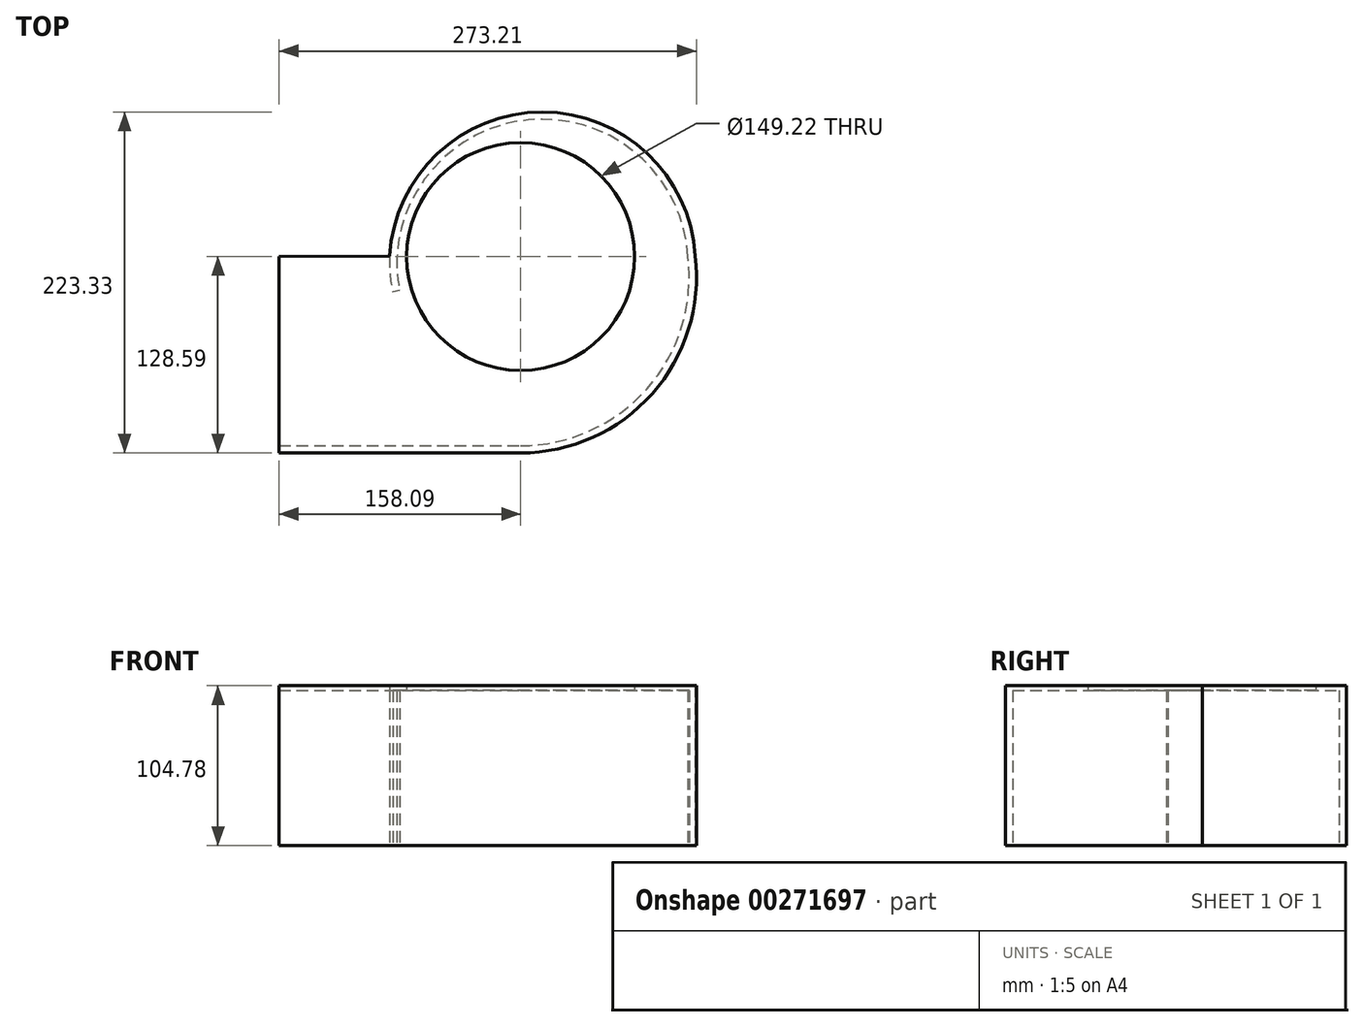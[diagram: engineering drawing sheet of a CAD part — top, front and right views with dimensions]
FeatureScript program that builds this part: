
annotation { "Feature Type Name" : "Feature", "Feature Type Description" : "" }
export const myFeature = defineFeature(function(context is Context, id is Id, definition is map)
    precondition{}
    {
        {
            var Q0;
            Q0=qCreatedBy(makeId("Top.planeOp"),FACE);
            var sketch = newSketch(context, id + "F3", { "sketchPlane" : qUnion([Q0])});
            skCircle(sketch, "E0", {"center": v(0, 0) * mm, "radius": 74.61 * mm, "construction": true});
            skPoint(sketch, "E1", {"position": v(-80.98, 0) * mm});
            skPoint(sketch, "E2", {"position": v(0, 88.9) * mm});
            skPoint(sketch, "E3", {"position": v(109.54, 0) * mm});
            skPoint(sketch, "E4", {"position": v(0, -123.83) * mm});
            skPoint(sketch, "E5", {"position": v(-138.11, 0) * mm});
            skArc(sketch, "E6", {"start": v(109.54, 0) * mm, "mid": v(14.28, 89.97) * mm, "end": v(-80.98, 0) * mm});
            skArc(sketch, "E7", {"start": v(-80.98, 0) * mm, "mid": v(-80.8, -11.18) * mm, "end": v(-79.04, -22.23) * mm});
            skLineSegment(sketch, "E8", {"start": v(-158.09, -123.83) * mm, "end": v(0, -123.83) * mm});
            skArc(sketch, "E9.trimOffspring", {"start": v(0, -123.83) * mm, "mid": v(82.66, -86.59) * mm, "end": v(109.54, 0) * mm});
            skArc(sketch, "E10.0", {"start": v(-85.73, 0.27) * mm, "mid": v(-85.55, -11.6) * mm, "end": v(-83.68, -23.31) * mm});
            skArc(sketch, "E10.1", {"start": v(114.28, 0.43) * mm, "mid": v(14.2, 94.74) * mm, "end": v(-85.73, 0.27) * mm});
            skArc(sketch, "E10.2", {"start": v(0, -128.59) * mm, "mid": v(86.18, -89.8) * mm, "end": v(114.28, 0.43) * mm});
            skLineSegment(sketch, "E11", {"start": v(-79.04, -22.23) * mm, "end": v(-83.68, -23.31) * mm});
            skPoint(sketch, "E12.end.orphan", {"position": v(-79.04, -123.83) * mm});
            skPoint(sketch, "E13.orphan", {"position": v(74.61, 0) * mm});
            skLineSegment(sketch, "E14.0", {"start": v(-158.09, -128.59) * mm, "end": v(0, -128.59) * mm});
            skLineSegment(sketch, "E15", {"start": v(-158.09, -128.59) * mm, "end": v(-158.09, -123.83) * mm});
            skSolve(sketch);
        }
        {
            var Q0;
            Q0=makeQuery(id+"F3.imprint","IMPRINT",FACE,{"disambiguationData":[TD([[makeQuery(id+"F3.imprint","IMPRINT",EDGE,{"derivedFrom":sQuery(id+"F3.wireOp",EDGE,"E6")}),-1.0]])]});
            var Q1;
            Q1=sQuery(id+"F3.wireOp",EDGE,"E10.1");
            var Q2;
            Q2=sQuery(id+"F3.wireOp",EDGE,"E6");
            var Q3;
            Q3=sQuery(id+"F3.wireOp",EDGE,"E9.trimOffspring");
            var Q4;
            Q4=sQuery(id+"F3.wireOp",EDGE,"E10.2");
            var Q5;
            Q5=sQuery(id+"F3.wireOp",EDGE,"E7");
            var Q6;
            Q6=sQuery(id+"F3.wireOp",EDGE,"E10.0");
            var Q7;
            Q7=sQuery(id+"F3.wireOp",EDGE,"E11");
            var Q8;
            Q8=sQuery(id+"F3.wireOp",EDGE,"E14.0");
            var Q9;
            Q9=sQuery(id+"F3.wireOp",EDGE,"E8");
            var Q10;
            Q10=sQuery(id+"F3.wireOp",EDGE,"E15");
            extrude(context, id + "F0", {"entities" : qUnion([Q0]), "surfaceEntities" : qUnion([Q1, Q2, Q3, Q4, Q5, Q6, Q7, Q8, Q9, Q10]), "depth" : 101.6 * mm});
        }
        {
            var Q0;
            Q0=makeQuery(id+"F0.opExtrude","CAP_FACE",FACE,{"disambiguationData":[OSD([sQuery(id+"F3.wireOp",EDGE,"E6"),sQuery(id+"F3.wireOp",EDGE,"E7"),sQuery(id+"F3.wireOp",EDGE,"E8"),sQuery(id+"F3.wireOp",EDGE,"E9.trimOffspring"),sQuery(id+"F3.wireOp",EDGE,"E10.0"),sQuery(id+"F3.wireOp",EDGE,"E10.1"),sQuery(id+"F3.wireOp",EDGE,"E10.2"),sQuery(id+"F3.wireOp",EDGE,"E11"),sQuery(id+"F3.wireOp",EDGE,"E14.0"),sQuery(id+"F3.wireOp",EDGE,"E15")])],"isStart":false});
            var sketch = newSketch(context, id + "F1", { "sketchPlane" : qUnion([Q0])});
            skArc(sketch, "E16", {"start": v(114.28, 0.43) * mm, "mid": v(14.2, 94.74) * mm, "end": v(-85.73, 0.27) * mm});
            skArc(sketch, "E17", {"start": v(0, -128.59) * mm, "mid": v(86.18, -89.8) * mm, "end": v(114.28, 0.43) * mm});
            skLineSegment(sketch, "E18", {"start": v(0, -128.59) * mm, "end": v(-158.09, -128.59) * mm});
            skLineSegment(sketch, "E19", {"start": v(-158.09, -128.59) * mm, "end": v(-158.09, 0) * mm});
            skLineSegment(sketch, "E20", {"start": v(-158.09, 0) * mm, "end": v(-85.73, 0.27) * mm});
            skCircle(sketch, "E21", {"center": v(0, 0) * mm, "radius": 74.61 * mm});
            skSolve(sketch);
        }
        {
            var Q0;
            Q0 = qSketchRegion(id + "F1", true);
            extrude(context, id + "F2", {"entities" : qUnion([Q0]), "operationType" : NewBodyOperationType.ADD, "depth" : 3.17 * mm});
        }
    });
